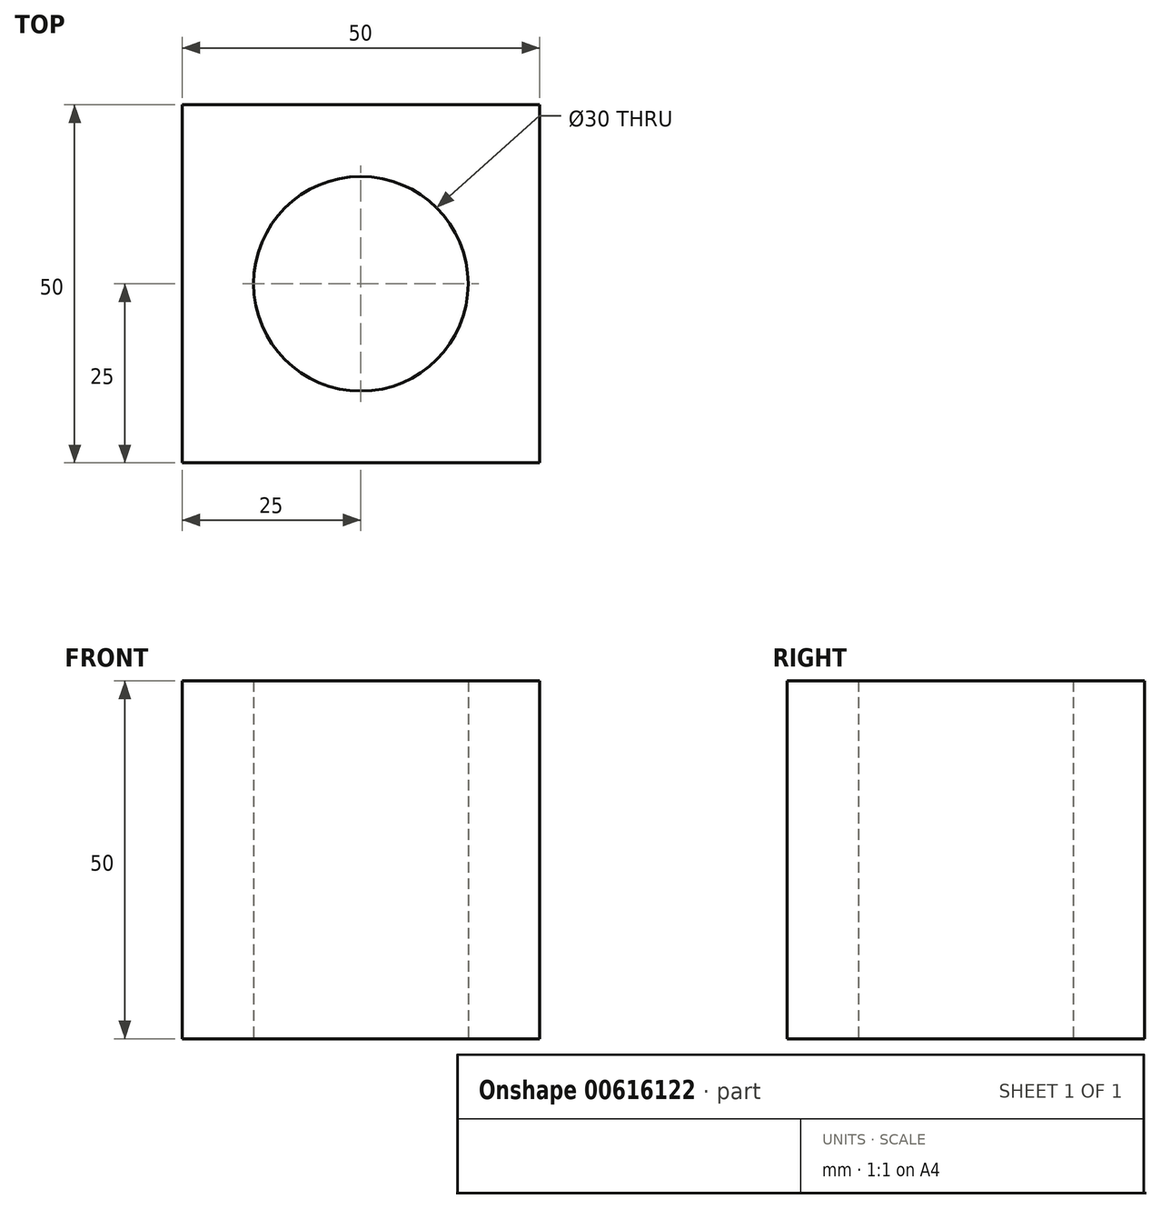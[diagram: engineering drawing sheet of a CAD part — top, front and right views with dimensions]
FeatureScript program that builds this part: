
annotation { "Feature Type Name" : "Feature", "Feature Type Description" : "" }
export const myFeature = defineFeature(function(context is Context, id is Id, definition is map)
    precondition{}
    {
        {
            var Q0;
            Q0=qCreatedBy(makeId("Top.planeOp"),FACE);
            var sketch = newSketch(context, id + "F0", { "sketchPlane" : qUnion([Q0])});
            skLineSegment(sketch, "E0.bottom", {"start": v(-25, 25) * mm, "end": v(25, 25) * mm});
            skLineSegment(sketch, "E0.top", {"start": v(-25, -25) * mm, "end": v(25, -25) * mm});
            skLineSegment(sketch, "E0.left", {"start": v(-25, 25) * mm, "end": v(-25, -25) * mm});
            skLineSegment(sketch, "E0.right", {"start": v(25, 25) * mm, "end": v(25, -25) * mm});
            skPoint(sketch, "E0.middle", {"position": v(0, 0) * mm});
            skSolve(sketch);
        }
        {
            var Q0;
            Q0 = qSketchRegion(id + "F0", true);
            extrude(context, id + "F1", {"entities" : qUnion([Q0]), "depth" : 50 * mm, "offsetDistance" : 25 * mm});
        }
        {
            var Q0;
            Q0=qCreatedBy(makeId("Top.planeOp"),FACE);
            var sketch = newSketch(context, id + "F2", { "sketchPlane" : qUnion([Q0])});
            skCircle(sketch, "E1", {"center": v(0, 0) * mm, "radius": 15 * mm});
            skSolve(sketch);
        }
        {
            var Q0;
            Q0 = qSketchRegion(id + "F2", true);
            extrude(context, id + "F3", {"entities" : qUnion([Q0]), "operationType" : NewBodyOperationType.REMOVE, "depth" : 50 * mm, "offsetDistance" : 25 * mm});
        }
    });
